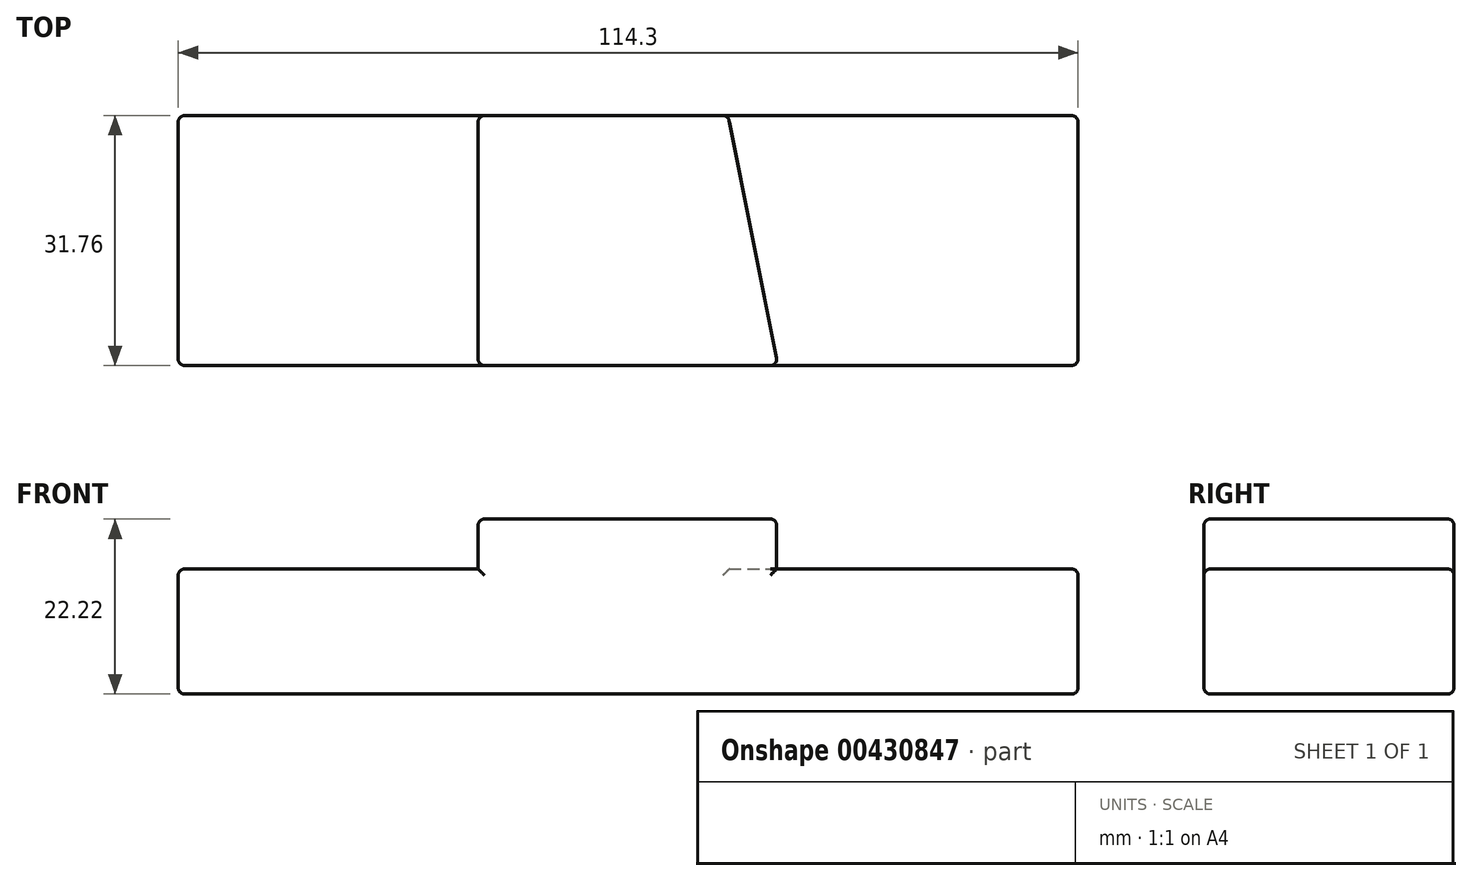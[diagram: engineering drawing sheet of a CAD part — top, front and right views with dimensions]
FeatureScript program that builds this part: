
annotation { "Feature Type Name" : "Feature", "Feature Type Description" : "" }
export const myFeature = defineFeature(function(context is Context, id is Id, definition is map)
    precondition{}
    {
        {
            var Q0;
            Q0=qCreatedBy(makeId("Top.planeOp"),FACE);
            var sketch = newSketch(context, id + "F0", { "sketchPlane" : qUnion([Q0])});
            skLineSegment(sketch, "E0.bottom", {"start": v(-57.15, -15.88) * mm, "end": v(57.15, -15.88) * mm});
            skLineSegment(sketch, "E0.top", {"start": v(-57.15, 15.88) * mm, "end": v(57.15, 15.88) * mm});
            skLineSegment(sketch, "E0.left", {"start": v(-57.15, -15.88) * mm, "end": v(-57.15, 15.88) * mm});
            skLineSegment(sketch, "E0.right", {"start": v(57.15, -15.88) * mm, "end": v(57.15, 15.88) * mm});
            skLineSegment(sketch, "E1", {"start": v(-57.15, 15.88) * mm, "end": v(57.15, -15.88) * mm, "construction": true});
            skSolve(sketch);
        }
        {
            var Q0;
            Q0 = qSketchRegion(id + "F0", true);
            extrude(context, id + "F1", {"entities" : qUnion([Q0]), "endBound" : BoundingType.SYMMETRIC, "depth" : 22.22 * mm});
        }
        {
            var Q0;
            Q0=makeQuery(id+"F1.opExtrude","CAP_FACE",FACE,{"disambiguationData":[OSD([sQuery(id+"F0.wireOp",EDGE,"E0.bottom"),sQuery(id+"F0.wireOp",EDGE,"E0.top"),sQuery(id+"F0.wireOp",EDGE,"E0.left"),sQuery(id+"F0.wireOp",EDGE,"E0.right")])],"isStart":false});
            var sketch = newSketch(context, id + "F2", { "sketchPlane" : qUnion([Q0])});
            skLineSegment(sketch, "E2.bottom", {"start": v(-57.15, 15.88) * mm, "end": v(-19.05, 15.88) * mm});
            skLineSegment(sketch, "E2.top", {"start": v(-57.15, -15.88) * mm, "end": v(-19.05, -15.88) * mm});
            skLineSegment(sketch, "E2.left", {"start": v(-57.15, 15.88) * mm, "end": v(-57.15, -15.88) * mm});
            skLineSegment(sketch, "E2.right", {"start": v(-19.05, 15.88) * mm, "end": v(-19.05, -15.88) * mm});
            skSolve(sketch);
        }
        {
            var Q0;
            Q0 = qSketchRegion(id + "F2", true);
            extrude(context, id + "F3", {"entities" : qUnion([Q0]), "operationType" : NewBodyOperationType.REMOVE, "oppositeDirection" : true, "depth" : 6.35 * mm});
        }
        {
            var Q0;
            Q0=makeQuery(id+"F1.opExtrude","CAP_FACE",FACE,{"disambiguationData":[OSD([sQuery(id+"F0.wireOp",EDGE,"E0.bottom"),sQuery(id+"F0.wireOp",EDGE,"E0.top"),sQuery(id+"F0.wireOp",EDGE,"E0.left"),sQuery(id+"F0.wireOp",EDGE,"E0.right")])],"isStart":false});
            var sketch = newSketch(context, id + "F4", { "sketchPlane" : qUnion([Q0])});
            skLineSegment(sketch, "E3", {"start": v(57.15, 15.88) * mm, "end": v(57.15, -15.88) * mm});
            skLineSegment(sketch, "E4", {"start": v(57.15, -15.88) * mm, "end": v(19.05, -15.88) * mm});
            skLineSegment(sketch, "E5", {"start": v(19.05, -15.88) * mm, "end": v(19.05, 111.12) * mm, "construction": true});
            skLineSegment(sketch, "E6", {"start": v(19.05, 111.12) * mm, "end": v(-6.35, 111.12) * mm, "construction": true});
            skLineSegment(sketch, "E7", {"start": v(19.05, -15.88) * mm, "end": v(-6.35, 111.12) * mm, "construction": true});
            skLineSegment(sketch, "E8", {"start": v(57.15, 15.88) * mm, "end": v(12.7, 15.88) * mm});
            skLineSegment(sketch, "E9", {"start": v(12.7, 15.88) * mm, "end": v(19.05, -15.88) * mm});
            skSolve(sketch);
        }
        {
            var Q0;
            Q0 = qSketchRegion(id + "F4", true);
            extrude(context, id + "F5", {"entities" : qUnion([Q0]), "operationType" : NewBodyOperationType.REMOVE, "oppositeDirection" : true, "depth" : 6.35 * mm});
        }
        {
            var Q0;
            Q0=makeQuery(id+"F1.opExtrude","CAP_FACE",FACE,{"disambiguationData":[OSD([sQuery(id+"F0.wireOp",EDGE,"E0.bottom"),sQuery(id+"F0.wireOp",EDGE,"E0.top"),sQuery(id+"F0.wireOp",EDGE,"E0.left"),sQuery(id+"F0.wireOp",EDGE,"E0.right")])],"isStart":false});
            var Q1;
            Q1=makeQuery(id+"F1.opExtrude","SWEPT_FACE",FACE,{"disambiguationData":[OSD([sQuery(id+"F0.wireOp",EDGE,"E0.bottom")])]});
            var Q2;
            Q2=makeQuery(id+"F1.opExtrude","SWEPT_FACE",FACE,{"disambiguationData":[OSD([sQuery(id+"F0.wireOp",EDGE,"E0.right")])]});
            var Q3;
            Q3=makeQuery(id+"F1.opExtrude","SWEPT_FACE",FACE,{"disambiguationData":[OSD([sQuery(id+"F0.wireOp",EDGE,"E0.top")])]});
            var Q4;
            Q4=makeQuery(id+"F1.opExtrude","CAP_FACE",FACE,{"disambiguationData":[OSD([sQuery(id+"F0.wireOp",EDGE,"E0.bottom"),sQuery(id+"F0.wireOp",EDGE,"E0.top"),sQuery(id+"F0.wireOp",EDGE,"E0.left"),sQuery(id+"F0.wireOp",EDGE,"E0.right")])],"isStart":true});
            var Q5;
            Q5=makeQuery(id+"F1.opExtrude","SWEPT_FACE",FACE,{"disambiguationData":[OSD([sQuery(id+"F0.wireOp",EDGE,"E0.left")])]});
            fillet(context, id + "F6", {"entities" : qUnion([Q0, Q1, Q2, Q3, Q4, Q5]), "radius" : 0.8 * mm, "tangentPropagation" : true, "allowEdgeOverflow" : false});
        }
    });
